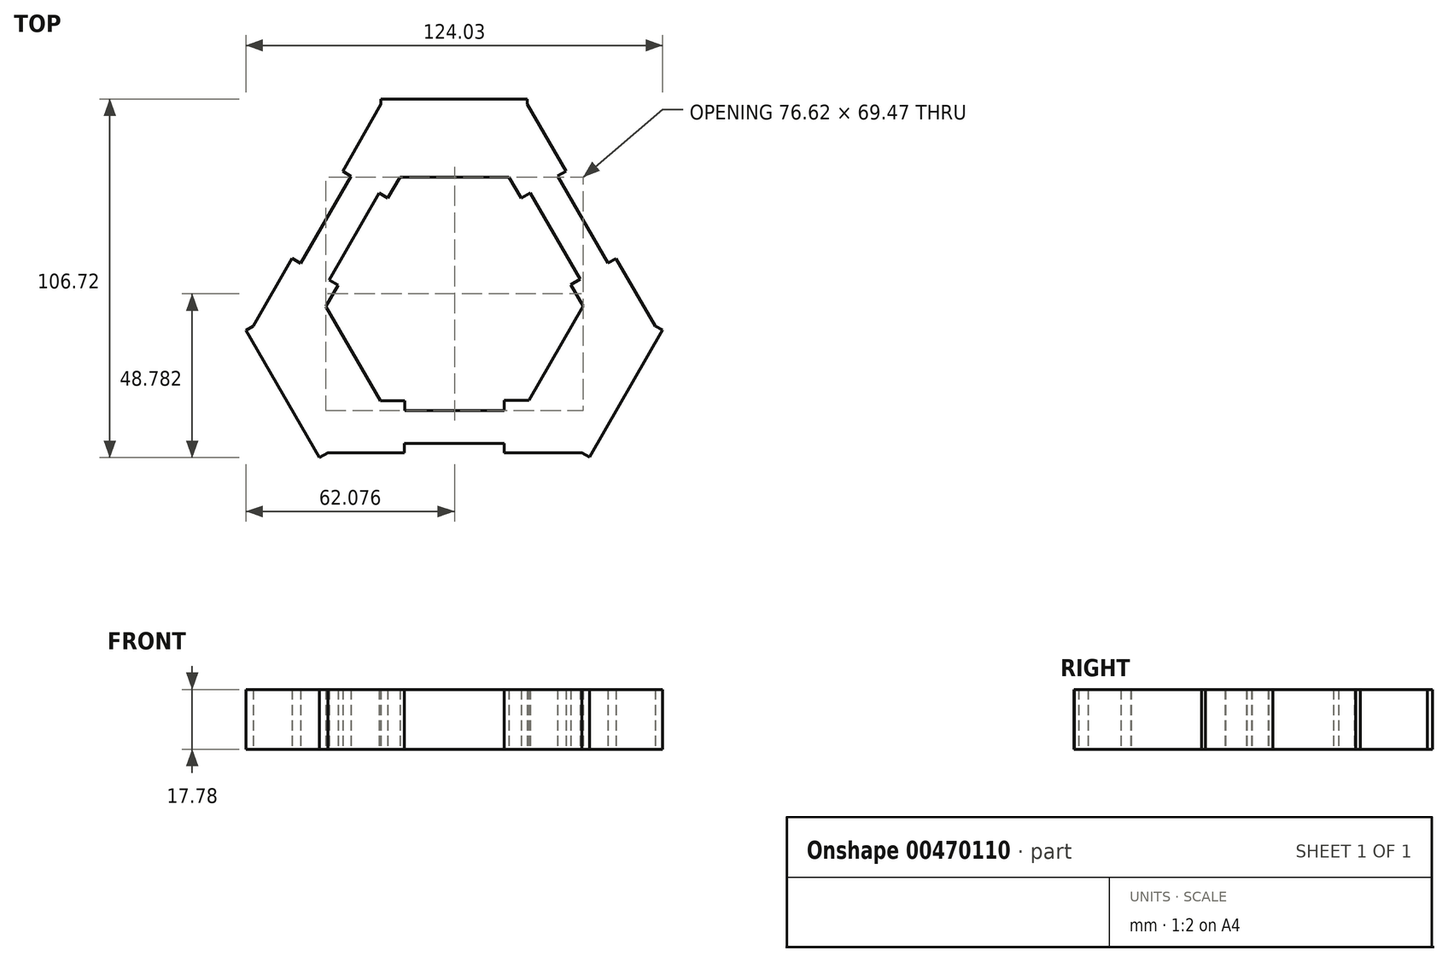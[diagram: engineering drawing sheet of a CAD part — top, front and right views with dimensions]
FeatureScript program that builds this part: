
annotation { "Feature Type Name" : "Feature", "Feature Type Description" : "" }
export const myFeature = defineFeature(function(context is Context, id is Id, definition is map)
    precondition{}
    {
        {
            var Q0;
            Q0=qCreatedBy(makeId("Top.planeOp"),FACE);
            var sketch = newSketch(context, id + "F0", { "sketchPlane" : qUnion([Q0])});
            skLineSegment(sketch, "E0", {"start": v(8.19, 120.46) * mm, "end": v(8.19, -105.51) * mm, "construction": true});
            skPoint(sketch, "E1", {"position": v(8.19, -45.81) * mm});
            skLineSegment(sketch, "E2", {"start": v(-25.08, 41.37) * mm, "end": v(-13.7, 61.29) * mm});
            skLineSegment(sketch, "E3", {"start": v(-13.7, 61.29) * mm, "end": v(-13.7, 62.82) * mm});
            skLineSegment(sketch, "E4", {"start": v(-13.7, 62.82) * mm, "end": v(29.85, 62.82) * mm});
            skLineSegment(sketch, "E5", {"start": v(29.85, 62.82) * mm, "end": v(29.85, 61.29) * mm});
            skLineSegment(sketch, "E6", {"start": v(29.85, 61.29) * mm, "end": v(41.35, 41.43) * mm});
            skLineSegment(sketch, "E7", {"start": v(41.35, 41.43) * mm, "end": v(38.8, 39.95) * mm});
            skLineSegment(sketch, "E8", {"start": v(38.8, 39.95) * mm, "end": v(53.84, 14) * mm});
            skLineSegment(sketch, "E9", {"start": v(53.84, 14) * mm, "end": v(56.25, 15.4) * mm});
            skLineSegment(sketch, "E10", {"start": v(56.25, 15.4) * mm, "end": v(67.9, -4.73) * mm});
            skLineSegment(sketch, "E11", {"start": v(67.9, -4.73) * mm, "end": v(70.12, -5.89) * mm});
            skLineSegment(sketch, "E12", {"start": v(70.12, -5.89) * mm, "end": v(48.38, -43.72) * mm});
            skLineSegment(sketch, "E13", {"start": v(48.38, -43.72) * mm, "end": v(46.08, -42.4) * mm});
            skLineSegment(sketch, "E14", {"start": v(46.08, -42.4) * mm, "end": v(23, -42.4) * mm});
            skLineSegment(sketch, "E15", {"start": v(23, -42.4) * mm, "end": v(23, -39.62) * mm});
            skLineSegment(sketch, "E16", {"start": v(23, -39.62) * mm, "end": v(-6.8, -39.62) * mm});
            skLineSegment(sketch, "E17", {"start": v(-6.8, -39.62) * mm, "end": v(-6.8, -42.4) * mm});
            skLineSegment(sketch, "E18", {"start": v(-6.8, -42.4) * mm, "end": v(-29.46, -42.4) * mm});
            skLineSegment(sketch, "E19", {"start": v(-29.46, -42.4) * mm, "end": v(-32.01, -43.9) * mm});
            skLineSegment(sketch, "E20", {"start": v(-32.01, -43.9) * mm, "end": v(-53.9, -6.02) * mm});
            skLineSegment(sketch, "E21", {"start": v(-53.9, -6.02) * mm, "end": v(-51.73, -4.76) * mm});
            skLineSegment(sketch, "E22", {"start": v(-51.73, -4.76) * mm, "end": v(-40.15, 15.4) * mm});
            skLineSegment(sketch, "E23", {"start": v(-40.15, 15.4) * mm, "end": v(-37.6, 13.93) * mm});
            skLineSegment(sketch, "E24", {"start": v(-37.6, 13.93) * mm, "end": v(-22.68, 39.9) * mm});
            skLineSegment(sketch, "E25", {"start": v(-22.68, 39.9) * mm, "end": v(-25.08, 41.37) * mm});
            skLineSegment(sketch, "E26", {"start": v(-8.02, 39.62) * mm, "end": v(24.35, 39.62) * mm});
            skLineSegment(sketch, "E27", {"start": v(24.35, 39.62) * mm, "end": v(27.97, 33.37) * mm});
            skLineSegment(sketch, "E28", {"start": v(27.97, 33.37) * mm, "end": v(30.68, 34.94) * mm});
            skLineSegment(sketch, "E29", {"start": v(30.68, 34.94) * mm, "end": v(45.6, 9.18) * mm});
            skLineSegment(sketch, "E30", {"start": v(45.6, 9.18) * mm, "end": v(42.8, 7.55) * mm});
            skLineSegment(sketch, "E31", {"start": v(42.8, 7.55) * mm, "end": v(46.48, 1.2) * mm});
            skLineSegment(sketch, "E32", {"start": v(46.48, 1.2) * mm, "end": v(30.36, -26.85) * mm});
            skLineSegment(sketch, "E33", {"start": v(30.36, -26.85) * mm, "end": v(23, -26.85) * mm});
            skLineSegment(sketch, "E34", {"start": v(23, -26.85) * mm, "end": v(23, -29.85) * mm});
            skLineSegment(sketch, "E35", {"start": v(23, -29.85) * mm, "end": v(-6.65, -29.85) * mm});
            skLineSegment(sketch, "E36", {"start": v(-6.65, -29.85) * mm, "end": v(-6.65, -26.96) * mm});
            skLineSegment(sketch, "E37", {"start": v(-6.65, -26.96) * mm, "end": v(-13.88, -26.96) * mm});
            skLineSegment(sketch, "E38", {"start": v(-13.88, -26.96) * mm, "end": v(-30.15, 1.12) * mm});
            skLineSegment(sketch, "E39", {"start": v(-30.15, 1.12) * mm, "end": v(-26.48, 7.5) * mm});
            skLineSegment(sketch, "E40", {"start": v(-26.48, 7.5) * mm, "end": v(-29.17, 9.04) * mm});
            skLineSegment(sketch, "E41", {"start": v(-29.17, 9.04) * mm, "end": v(-14.3, 34.9) * mm});
            skLineSegment(sketch, "E42", {"start": v(-14.3, 34.9) * mm, "end": v(-11.7, 33.42) * mm});
            skLineSegment(sketch, "E43", {"start": v(-11.7, 33.42) * mm, "end": v(-8.02, 39.62) * mm});
            skSolve(sketch);
        }
        {
            var Q0;
            Q0=makeQuery(id+"F0.imprint","IMPRINT",FACE,{"disambiguationData":[TD([[makeQuery(id+"F0.imprint","IMPRINT",EDGE,{"derivedFrom":sQuery(id+"F0.wireOp",EDGE,"E2")}),-1.0]])]});
            extrude(context, id + "F1", {"entities" : qUnion([Q0]), "depth" : 17.78 * mm});
        }
    });
